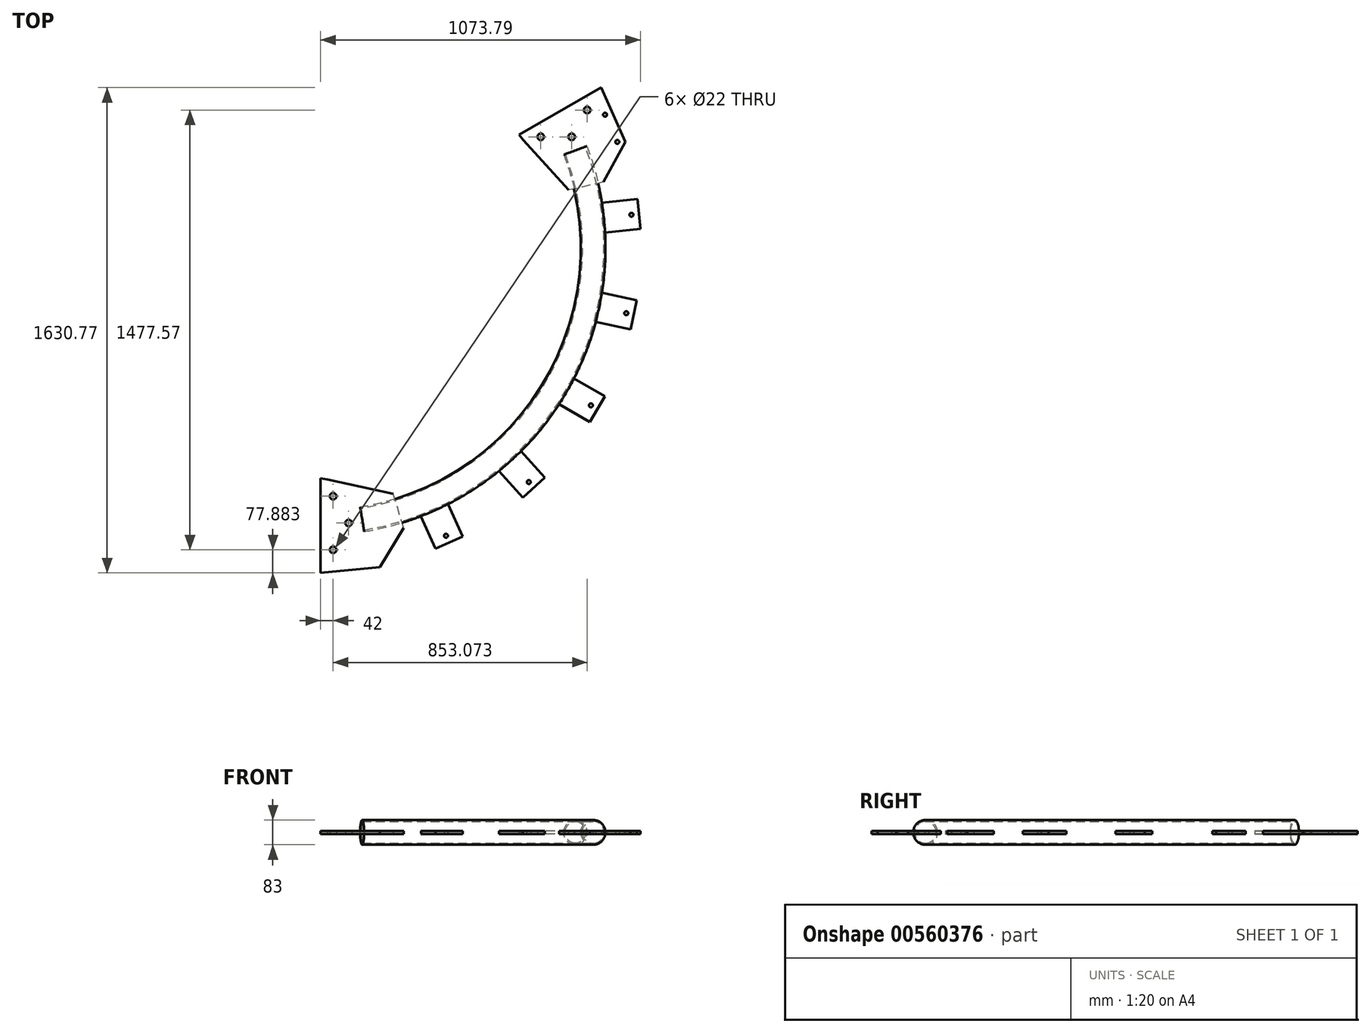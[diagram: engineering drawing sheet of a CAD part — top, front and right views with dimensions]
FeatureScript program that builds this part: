
annotation { "Feature Type Name" : "Feature", "Feature Type Description" : "" }
export const myFeature = defineFeature(function(context is Context, id is Id, definition is map)
    precondition{}
    {
        {
            var Q0;
            Q0=qCreatedBy(makeId("Top.planeOp"),FACE);
            var sketch = newSketch(context, id + "F0", { "sketchPlane" : qUnion([Q0])});
            skCircle(sketch, "E0", {"center": v(0, 0) * mm, "radius": 1100 * mm, "construction": true});
            skArc(sketch, "E1", {"start": v(149.5, -912.84) * mm, "mid": v(801.07, -462.5) * mm, "end": v(865.3, 326.94) * mm});
            skLineSegment(sketch, "E2", {"start": v(0, 0) * mm, "end": v(0, -775) * mm, "construction": true});
            skArc(sketch, "E3", {"start": v(0, -775) * mm, "mid": v(-5, -1074.92) * mm, "end": v(10, -775.33) * mm, "construction": true});
            skLineSegment(sketch, "E4", {"start": v(0, 0) * mm, "end": v(1095.31, 632.38) * mm, "construction": true});
            skCircle(sketch, "E5", {"center": v(801.07, 462.5) * mm, "radius": 150 * mm, "construction": true});
            skLineSegment(sketch, "E6", {"start": v(289.1, -941.62) * mm, "end": v(253.88, -826.9) * mm});
            skLineSegment(sketch, "E7", {"start": v(208.99, -1072.83) * mm, "end": v(289.1, -941.62) * mm});
            skLineSegment(sketch, "E8", {"start": v(253.88, -826.9) * mm, "end": v(32, -778.45) * mm});
            skLineSegment(sketch, "E9", {"start": v(208.99, -1072.83) * mm, "end": v(10, -1092.95) * mm});
            skLineSegment(sketch, "E10", {"start": v(0, 0) * mm, "end": v(801.07, -462.5) * mm, "construction": true});
            skLineSegment(sketch, "E11.MirrorCS", {"start": v(843.06, 193.58) * mm, "end": v(690.16, 361.51) * mm});
            skLineSegment(sketch, "E12.MirrorCS", {"start": v(676.46, 379) * mm, "end": v(951.53, 537.82) * mm});
            skLineSegment(sketch, "E13.MirrorCS", {"start": v(1033.6, 355.43) * mm, "end": v(951.53, 537.82) * mm});
            skLineSegment(sketch, "E14.MirrorCS", {"start": v(1033.6, 355.43) * mm, "end": v(960.02, 220.44) * mm});
            skLineSegment(sketch, "E15.MirrorCS", {"start": v(960.02, 220.44) * mm, "end": v(843.06, 193.58) * mm});
            skCircle(sketch, "E16.cCircle", {"center": v(0, -925) * mm, "radius": 104 * mm, "construction": true});
            skLineSegment(sketch, "E16.0", {"start": v(-52, -834.93) * mm, "end": v(52, -834.93) * mm, "construction": true});
            skLineSegment(sketch, "E16.1", {"start": v(52, -834.93) * mm, "end": v(104, -925) * mm, "construction": true});
            skLineSegment(sketch, "E16.2", {"start": v(104, -925) * mm, "end": v(52, -1015.07) * mm, "construction": true});
            skLineSegment(sketch, "E16.3", {"start": v(52, -1015.07) * mm, "end": v(-52, -1015.07) * mm, "construction": true});
            skLineSegment(sketch, "E16.4", {"start": v(-52, -1015.07) * mm, "end": v(-104, -925) * mm, "construction": true});
            skLineSegment(sketch, "E16.5", {"start": v(-104, -925) * mm, "end": v(-52, -834.93) * mm, "construction": true});
            skCircle(sketch, "E17", {"center": v(52, -834.93) * mm, "radius": 11 * mm});
            skCircle(sketch, "E18", {"center": v(104, -925) * mm, "radius": 11 * mm});
            skCircle(sketch, "E19", {"center": v(52, -1015.07) * mm, "radius": 11 * mm});
            skCircle(sketch, "E20.MirrorC", {"center": v(853.07, 372.43) * mm, "radius": 11 * mm});
            skCircle(sketch, "E21.MirrorC", {"center": v(749.07, 372.43) * mm, "radius": 11 * mm});
            skCircle(sketch, "E22.MirrorC", {"center": v(905.07, 462.5) * mm, "radius": 11 * mm});
            skLineSegment(sketch, "E23", {"start": v(10, -1092.95) * mm, "end": v(10, -775.33) * mm});
            skLineSegment(sketch, "E24", {"start": v(32, -778.45) * mm, "end": v(10, -775.33) * mm});
            skLineSegment(sketch, "E25", {"start": v(690.16, 361.51) * mm, "end": v(676.46, 379) * mm});
            skSolve(sketch);
        }
        {
            var Q0;
            Q0=sQuery(id+"F0.wireOp",VERTEX,"E1.end");
            var Q1;
            Q1=sQuery(id+"F0.wireOp",EDGE,"E1");
            cPlane(context, id + "F1", {"entities" : qUnion([Q0, Q1]), "cplaneType" : CPlaneType.CURVE_POINT, "offset" : 25 * mm, "width" : 150 * mm, "height" : 150 * mm});
        }
        {
            var Q0;
            Q0=makeQuery(id+"F0.imprint","IMPRINT",FACE,{"disambiguationData":[TD([[makeQuery(id+"F0.imprint","IMPRINT",EDGE,{"derivedFrom":sQuery(id+"F0.wireOp",EDGE,"E11.MirrorCS")}),-1.0]])]});
            var Q1;
            Q1=makeQuery(id+"F0.imprint","IMPRINT",FACE,{"disambiguationData":[TD([[makeQuery(id+"F0.imprint","IMPRINT",EDGE,{"derivedFrom":sQuery(id+"F0.wireOp",EDGE,"E6")}),1.0]])]});
            extrude(context, id + "F2", {"entities" : qUnion([Q0, Q1]), "endBound" : BoundingType.SYMMETRIC, "depth" : 10 * mm, "offsetDistance" : 25 * mm});
        }
        {
            var Q0;
            Q0=qCreatedBy(id+"F1.planeOp",FACE);
            var sketch = newSketch(context, id + "F3", { "sketchPlane" : qUnion([Q0])});
            skCircle(sketch, "E26", {"center": v(-925, 0) * mm, "radius": 41.5 * mm});
            skCircle(sketch, "E27", {"center": v(-925, 0) * mm, "radius": 36.5 * mm});
            skSolve(sketch);
        }
        {
            var Q0;
            Q0 = qSketchRegion(id + "F3", true);
            var Q1;
            Q1=sQuery(id+"F0.wireOp",EDGE,"E1");
            sweep(context, id + "F4", {"profiles" : qUnion([Q0]), "path" : qUnion([Q1])});
        }
        {
            var Q0;
            Q0=makeQuery(id+"F2.opExtrude","CAP_FACE",FACE,{"disambiguationData":[OSD([sQuery(id+"F0.wireOp",EDGE,"E11.MirrorCS"),sQuery(id+"F0.wireOp",EDGE,"E12.MirrorCS"),sQuery(id+"F0.wireOp",EDGE,"E13.MirrorCS"),sQuery(id+"F0.wireOp",EDGE,"E14.MirrorCS"),sQuery(id+"F0.wireOp",EDGE,"E15.MirrorCS"),sQuery(id+"F0.wireOp",EDGE,"95a24cb5-3592-498c-b9ac-72a86bf24bc80.MirrorC"),sQuery(id+"F0.wireOp",EDGE,"056990ec-4dff-4604-b14d-059e47948b030.MirrorC")])],"isStart":true});
            var sketch = newSketch(context, id + "F5", { "sketchPlane" : qUnion([Q0])});
            skCircle(sketch, "E28", {"center": v(965.15, -446.62) * mm, "radius": 6.5 * mm});
            skPoint(sketch, "E28.centerSnap0", {"position": v(992.56, -446.62) * mm});
            skCircle(sketch, "E29", {"center": v(1006.18, -355.43) * mm, "radius": 6.5 * mm});
            skLineSegment(sketch, "E30", {"start": v(965.15, -446.62) * mm, "end": v(1006.18, -355.43) * mm, "construction": true});
            skCircle(sketch, "E31.MirrorC", {"center": v(95.79, 1059.15) * mm, "radius": 6.5 * mm});
            skCircle(sketch, "E32.MirrorC", {"center": v(195.28, 1049.1) * mm, "radius": 6.5 * mm});
            skSolve(sketch);
        }
        {
            var Q0;
            Q0=makeQuery(id+"F5.imprint","IMPRINT",FACE,{"disambiguationData":[TD([[makeQuery(id+"F5.imprint","IMPRINT",EDGE,{"derivedFrom":sQuery(id+"F5.wireOp",EDGE,"E31.MirrorC")}),-1.0]])]});
            var Q1;
            Q1=makeQuery(id+"F5.imprint","IMPRINT",FACE,{"disambiguationData":[TD([[makeQuery(id+"F5.imprint","IMPRINT",EDGE,{"derivedFrom":sQuery(id+"F5.wireOp",EDGE,"E32.MirrorC")}),-1.0]])]});
            var Q2;
            Q2=makeQuery(id+"F5.imprint","IMPRINT",FACE,{"disambiguationData":[TD([[makeQuery(id+"F5.imprint","IMPRINT",EDGE,{"derivedFrom":sQuery(id+"F5.wireOp",EDGE,"E29")}),1.0]])]});
            var Q3;
            Q3=makeQuery(id+"F5.imprint","IMPRINT",FACE,{"disambiguationData":[TD([[makeQuery(id+"F5.imprint","IMPRINT",EDGE,{"derivedFrom":sQuery(id+"F5.wireOp",EDGE,"E28")}),1.0]])]});
            var Q4;
            Q4=sQuery(id+"F5.wireOp",EDGE,"E30");
            var Q5;
            Q5=sQuery(id+"F5.wireOp",EDGE,"E29");
            var Q6;
            Q6=sQuery(id+"F5.wireOp",EDGE,"E28");
            var Q7;
            Q7=sQuery(id+"F5.wireOp",EDGE,"E31.MirrorC");
            var Q8;
            Q8=sQuery(id+"F5.wireOp",EDGE,"E32.MirrorC");
            extrude(context, id + "F6", {"entities" : qUnion([Q0, Q1, Q2, Q3]), "operationType" : NewBodyOperationType.REMOVE, "surfaceEntities" : qUnion([Q4, Q5, Q6, Q7, Q8]), "oppositeDirection" : true, "depth" : 25 * mm, "offsetDistance" : 25 * mm});
        }
        {
            var Q0;
            Q0=qCreatedBy(makeId("Top.planeOp"),FACE);
            var sketch = newSketch(context, id + "F7", { "sketchPlane" : qUnion([Q0])});
            skLineSegment(sketch, "E33", {"start": v(860.28, -438.95) * mm, "end": v(964.2, -498.95) * mm});
            skLineSegment(sketch, "E34", {"start": v(964.2, -498.95) * mm, "end": v(914.2, -585.55) * mm});
            skLineSegment(sketch, "E35", {"start": v(914.2, -585.55) * mm, "end": v(810.28, -525.55) * mm});
            skLineSegment(sketch, "E36", {"start": v(810.28, -525.55) * mm, "end": v(835.28, -482.25) * mm, "construction": true});
            skLineSegment(sketch, "E37", {"start": v(0, 0) * mm, "end": v(939.2, -542.25) * mm, "construction": true});
            skArc(sketch, "E38", {"start": v(809.16, -524.9) * mm, "mid": v(835.28, -482.25) * mm, "end": v(859.16, -438.3) * mm});
            skLineSegment(sketch, "E39", {"start": v(860.28, -438.95) * mm, "end": v(859.16, -438.3) * mm});
            skLineSegment(sketch, "E40", {"start": v(810.28, -525.55) * mm, "end": v(809.16, -524.9) * mm});
            skLineSegment(sketch, "E41", {"start": v(0, 0) * mm, "end": v(538.35, -435.95) * mm, "construction": true});
            skLineSegment(sketch, "E42", {"start": v(0, 0) * mm, "end": v(594.82, -228.33) * mm, "construction": true});
            skCircle(sketch, "E43", {"center": v(917.55, -529.75) * mm, "radius": 6.5 * mm});
            skCircle(sketch, "E44.MirrorC", {"center": v(1036.35, -220.28) * mm, "radius": 6.5 * mm});
            skLineSegment(sketch, "E45.MirrorCS", {"start": v(933.03, -249.44) * mm, "end": v(1050.4, -274.39) * mm});
            skLineSegment(sketch, "E46.MirrorCS", {"start": v(1050.4, -274.39) * mm, "end": v(1071.2, -176.57) * mm});
            skLineSegment(sketch, "E47.MirrorCS", {"start": v(1071.2, -176.57) * mm, "end": v(953.82, -151.62) * mm});
            skArc(sketch, "E48.MirrorCS", {"start": v(952.55, -151.35) * mm, "mid": v(943.42, -200.53) * mm, "end": v(931.76, -249.17) * mm});
            skLineSegment(sketch, "E49.MirrorCS", {"start": v(953.82, -151.62) * mm, "end": v(952.55, -151.35) * mm});
            skLineSegment(sketch, "E50.MirrorCS", {"start": v(933.03, -249.44) * mm, "end": v(931.76, -249.17) * mm});
            skArc(sketch, "E51.MirrorCS", {"start": v(681.67, -682.34) * mm, "mid": v(645.38, -716.76) * mm, "end": v(607.35, -749.26) * mm});
            skLineSegment(sketch, "E52.MirrorCS", {"start": v(608.22, -750.22) * mm, "end": v(607.35, -749.26) * mm});
            skLineSegment(sketch, "E53.MirrorCS", {"start": v(608.22, -750.22) * mm, "end": v(688.51, -839.4) * mm});
            skLineSegment(sketch, "E54.MirrorCS", {"start": v(762.83, -772.48) * mm, "end": v(682.53, -683.3) * mm});
            skLineSegment(sketch, "E55.MirrorCS", {"start": v(688.51, -839.4) * mm, "end": v(762.83, -772.48) * mm});
            skCircle(sketch, "E56.MirrorC", {"center": v(708.94, -787.36) * mm, "radius": 6.5 * mm});
            skLineSegment(sketch, "E57", {"start": v(682.53, -683.3) * mm, "end": v(681.67, -682.34) * mm});
            skLineSegment(sketch, "E58", {"start": v(0, 0) * mm, "end": v(708.94, -787.36) * mm, "construction": true});
            skLineSegment(sketch, "E59", {"start": v(0, 0) * mm, "end": v(559.33, -861.29) * mm, "construction": true});
            skLineSegment(sketch, "E60.MirrorCS", {"start": v(346.62, -901.45) * mm, "end": v(346.1, -900.27) * mm});
            skLineSegment(sketch, "E61.MirrorCS", {"start": v(437.97, -860.78) * mm, "end": v(437.45, -859.6) * mm});
            skCircle(sketch, "E62.MirrorC", {"center": v(430.94, -967.9) * mm, "radius": 6.5 * mm});
            skLineSegment(sketch, "E63.MirrorCS", {"start": v(395.43, -1011.08) * mm, "end": v(346.62, -901.45) * mm});
            skArc(sketch, "E64.MirrorCS", {"start": v(346.1, -900.27) * mm, "mid": v(392.3, -881.11) * mm, "end": v(437.45, -859.6) * mm});
            skLineSegment(sketch, "E65.MirrorCS", {"start": v(486.78, -970.4) * mm, "end": v(395.43, -1011.08) * mm});
            skLineSegment(sketch, "E66.MirrorCS", {"start": v(437.97, -860.78) * mm, "end": v(486.78, -970.4) * mm});
            skLineSegment(sketch, "E67", {"start": v(1036.35, -220.28) * mm, "end": v(0, 0) * mm, "construction": true});
            skLineSegment(sketch, "E68", {"start": v(0, 0) * mm, "end": v(1010.3, -52.95) * mm, "construction": true});
            skLineSegment(sketch, "E69.MirrorCS", {"start": v(953.99, 150.54) * mm, "end": v(952.7, 150.4) * mm});
            skLineSegment(sketch, "E70.MirrorCS", {"start": v(964.44, 51.1) * mm, "end": v(963.15, 50.96) * mm});
            skCircle(sketch, "E71.MirrorC", {"center": v(1053.7, 110.75) * mm, "radius": 6.5 * mm});
            skLineSegment(sketch, "E72.MirrorCS", {"start": v(953.99, 150.54) * mm, "end": v(1073.33, 163.09) * mm});
            skLineSegment(sketch, "E73.MirrorCS", {"start": v(1083.79, 63.64) * mm, "end": v(964.44, 51.1) * mm});
            skArc(sketch, "E74.MirrorCS", {"start": v(963.15, 50.96) * mm, "mid": v(959.22, 100.82) * mm, "end": v(952.7, 150.4) * mm});
            skLineSegment(sketch, "E75.MirrorCS", {"start": v(1073.33, 163.09) * mm, "end": v(1083.79, 63.64) * mm});
            skSolve(sketch);
        }
        {
            var Q0;
            Q0 = qSketchRegion(id + "F7", true);
            extrude(context, id + "F8", {"entities" : qUnion([Q0]), "operationType" : NewBodyOperationType.ADD, "endBound" : BoundingType.SYMMETRIC, "depth" : 10 * mm, "offsetDistance" : 25 * mm});
        }
    });
